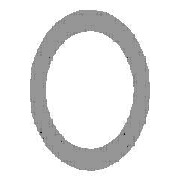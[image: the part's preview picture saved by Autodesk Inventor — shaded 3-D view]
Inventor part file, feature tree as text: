
AUTODESK INVENTOR PART (.ipt)
format: ipt  version: 2013 (Build 170138000, 138)  size: 114,176 bytes
history: native  units: mm (DEFAULTED — no unit token found)
features: other x4, sketch x3, plane x2, split x1
ambient origin geometry x8: Origin, YZ Plane, XZ Plane, XY Plane, X Axis, Y Axis, Z Axis, Center Point
bodies: Solid1 (feature_tree), Body (feature_tree)
feature tree (10):
  parser-record x1  (decoder bookkeeping rows leaked as tree rows — omitted from the tree; the rows remain in map.json)
  other  "Driven Length"
  other  "Start plane"
  other  "End plane"
  plane  "Work Plane4"
  split  "Split1"
  sketch  "Sketch"  dims[d2=541.401mm d3=0.0mm d4=-33.401mm d5=508.0mm d6=90.0deg d7=541.401mm]
  sketch  "Sketch3"  dims[d0=33.401mm]
  plane  "Work Plane3"
  sketch  "Sketch4"  dims[d1=3.3782mm]
